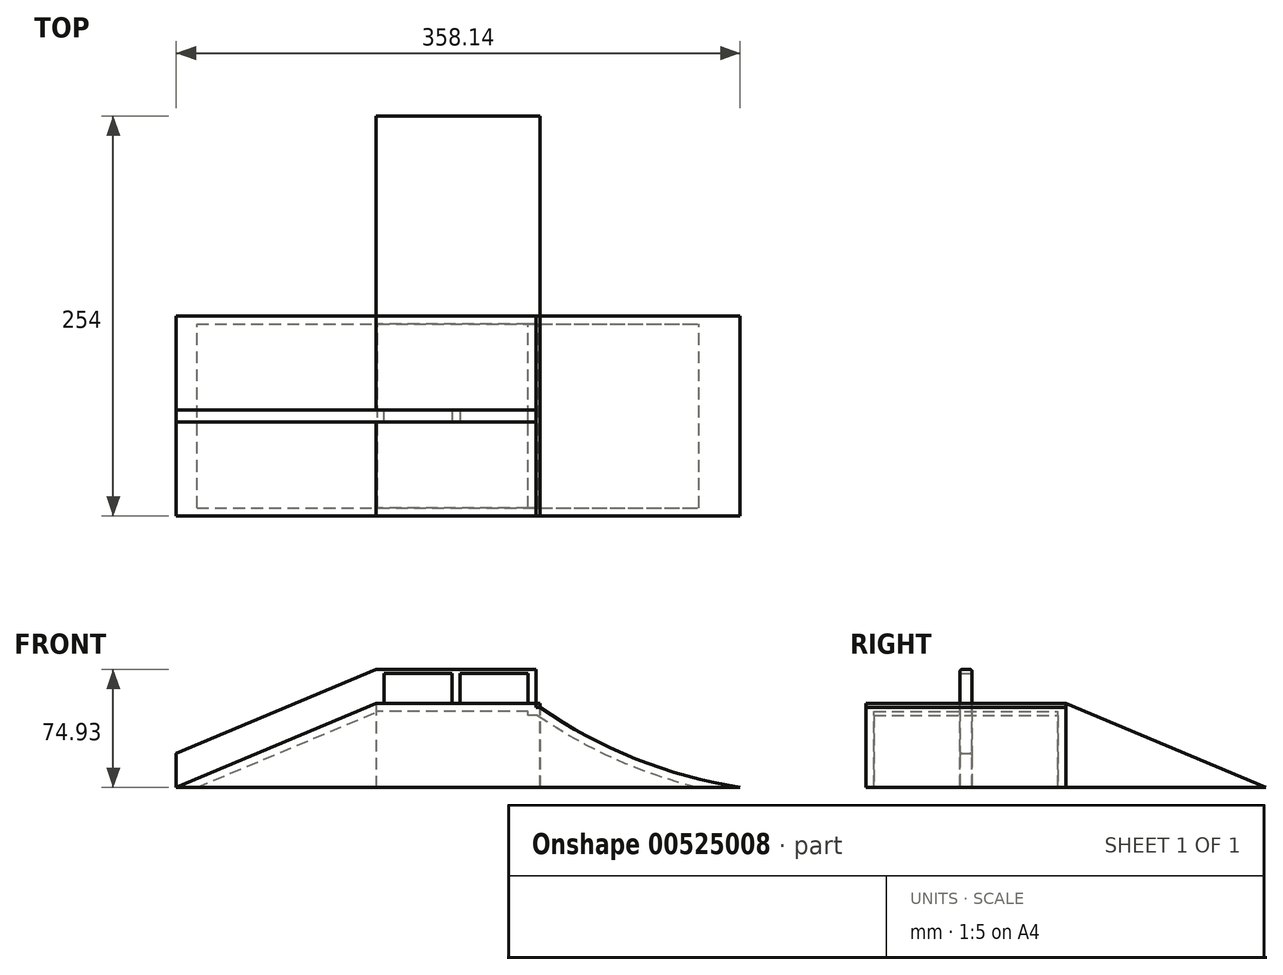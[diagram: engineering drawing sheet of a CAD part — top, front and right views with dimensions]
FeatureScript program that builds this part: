
annotation { "Feature Type Name" : "Feature", "Feature Type Description" : "" }
export const myFeature = defineFeature(function(context is Context, id is Id, definition is map)
    precondition{}
    {
        {
            var Q0;
            Q0=qCreatedBy(makeId("Front.planeOp"),FACE);
            var sketch = newSketch(context, id + "F0", { "sketchPlane" : qUnion([Q0])});
            skLineSegment(sketch, "E0.bottom", {"start": v(0, 0) * mm, "end": v(127, 0) * mm});
            skLineSegment(sketch, "E0.left", {"start": v(0, 0) * mm, "end": v(0, 50.8) * mm});
            skArc(sketch, "E1", {"start": v(0, 50.8) * mm, "mid": v(60.61, 18.18) * mm, "end": v(127, 0) * mm});
            skLineSegment(sketch, "E2.bottom", {"start": v(0, 0) * mm, "end": v(-2.54, 0) * mm});
            skLineSegment(sketch, "E2.top", {"start": v(0, 50.8) * mm, "end": v(-2.54, 50.8) * mm});
            skLineSegment(sketch, "E2.right", {"start": v(-2.54, 0) * mm, "end": v(-2.54, 50.8) * mm});
            skLineSegment(sketch, "E3.bottom", {"start": v(-2.54, 0) * mm, "end": v(-104.14, 0) * mm});
            skLineSegment(sketch, "E3.top", {"start": v(-2.54, 53.34) * mm, "end": v(-104.14, 53.34) * mm});
            skLineSegment(sketch, "E3.left", {"start": v(-2.54, 0) * mm, "end": v(-2.54, 53.34) * mm});
            skLineSegment(sketch, "E3.right", {"start": v(-104.14, 0) * mm, "end": v(-104.14, 53.34) * mm});
            skCircle(sketch, "E4", {"center": v(-1.27, 52.07) * mm, "radius": 1.27 * mm});
            skPoint(sketch, "E4.centerSnap0", {"position": v(-1.27, 50.8) * mm});
            skLineSegment(sketch, "E5", {"start": v(-104.14, 0) * mm, "end": v(-231.14, 0) * mm});
            skLineSegment(sketch, "E6", {"start": v(-231.14, 0) * mm, "end": v(-104.14, 53.34) * mm});
            skSolve(sketch);
        }
        {
            var Q0;
            Q0=makeQuery(id+"F0.imprint","IMPRINT",FACE,{"disambiguationData":[TD([[makeQuery(id+"F0.imprint","IMPRINT",EDGE,{"derivedFrom":sQuery(id+"F0.wireOp",EDGE,"E0.bottom")}),1.0]])]});
            var Q1;
            Q1=makeQuery(id+"F0.imprint","IMPRINT",FACE,{"disambiguationData":[TD([[makeQuery(id+"F0.imprint","IMPRINT",EDGE,{"derivedFrom":sQuery(id+"F0.wireOp",EDGE,"gSf4ow2M-3nON-57kk-JyT3-ZSVy4p9OPfto.bottom")}),-1.0]])]});
            var Q2;
            {var subQ3=sQuery(id+"F0.wireOp",EDGE,"E3.bottom");Q2=makeQuery(id+"F0.imprint","IMPRINT",FACE,{"disambiguationData":[TD([[makeQuery(id+"F0.imprint","IMPRINT",EDGE,{"derivedFrom":subQ3}),-1.0]])]});}
            var Q3;
            {var subQ5=sQuery(id+"F0.wireOp",EDGE,"E2.bottom");Q3=makeQuery(id+"F0.imprint","IMPRINT",FACE,{"disambiguationData":[TD([[makeQuery(id+"F0.imprint","IMPRINT",EDGE,{"derivedFrom":subQ5}),-1.0]])]});}
            var Q4;
            {var subQ0=sQuery(id+"F0.wireOp",EDGE,"E4");var subQ1=makeQuery(id+"F0.imprint","INTERSECT",VERTEX,{"derivedFrom":[sQuery(id+"F0.wireOp",EDGE,"E2.top"),subQ0]});Q4=makeQuery(id+"F0.imprint","IMPRINT",FACE,{"disambiguationData":[TD([[makeQuery(id+"F0.imprint","IMPRINT",EDGE,{"disambiguationData":[TD([[subQ1,1.0]])],"derivedFrom":subQ0}),1.0]])]});}
            var Q5;
            Q5=makeQuery(id+"F0.imprint","IMPRINT",FACE,{"disambiguationData":[TD([[makeQuery(id+"F0.imprint","IMPRINT",EDGE,{"derivedFrom":sQuery(id+"F0.wireOp",EDGE,"E3.right")}),1.0]])]});
            extrude(context, id + "F1", {"entities" : qUnion([Q0, Q1, Q2, Q3, Q4, Q5]), "depth" : 127 * mm});
        }
        {
            var Q0;
            Q0=makeQuery(id+"F1.opExtrude","SWEPT_FACE",FACE,{"disambiguationData":[OSD([sQuery(id+"F0.wireOp",EDGE,"E3.top")])]});
            var sketch = newSketch(context, id + "F2", { "sketchPlane" : qUnion([Q0])});
            skLineSegment(sketch, "E7.bottom", {"start": v(-104.14, -67.31) * mm, "end": v(-99.06, -67.31) * mm});
            skLineSegment(sketch, "E7.top", {"start": v(-104.14, -59.7) * mm, "end": v(-99.06, -59.7) * mm});
            skLineSegment(sketch, "E7.left", {"start": v(-104.14, -67.31) * mm, "end": v(-104.14, -59.7) * mm});
            skLineSegment(sketch, "E7.right", {"start": v(-99.06, -67.31) * mm, "end": v(-99.06, -59.7) * mm});
            skLineSegment(sketch, "E8.bottom", {"start": v(-2.54, -67.3) * mm, "end": v(-7.62, -67.3) * mm});
            skLineSegment(sketch, "E8.top", {"start": v(-2.54, -59.7) * mm, "end": v(-7.62, -59.7) * mm});
            skLineSegment(sketch, "E8.left", {"start": v(-2.54, -67.3) * mm, "end": v(-2.54, -59.7) * mm});
            skLineSegment(sketch, "E8.right", {"start": v(-7.62, -67.3) * mm, "end": v(-7.62, -59.7) * mm});
            skLineSegment(sketch, "E9.bottom", {"start": v(-55.88, -59.7) * mm, "end": v(-50.8, -59.7) * mm});
            skLineSegment(sketch, "E9.top", {"start": v(-55.88, -67.31) * mm, "end": v(-50.8, -67.31) * mm});
            skLineSegment(sketch, "E9.left", {"start": v(-55.88, -59.7) * mm, "end": v(-55.88, -67.31) * mm});
            skLineSegment(sketch, "E9.right", {"start": v(-50.8, -59.7) * mm, "end": v(-50.8, -67.31) * mm});
            skSolve(sketch);
        }
        {
            var Q0;
            Q0=qSketchRegion(id+"F2",true);
            extrude(context, id + "F3", {"entities" : qUnion([Q0]), "operationType" : NewBodyOperationType.ADD, "depth" : 19.05 * mm});
        }
        {
            var Q0;
            Q0=makeQuery(id+"F3.boolean.opBoolean","MERGE",FACE,{"derivedFrom":[makeQuery(id+"F1.opExtrude","SWEPT_FACE",FACE,{"disambiguationData":[OSD([sQuery(id+"F0.wireOp",EDGE,"E3.left")])]}),makeQuery(id+"F3.opExtrude","SWEPT_FACE",FACE,{"disambiguationData":[OSD([sQuery(id+"F2.wireOp",EDGE,"E8.left")])]})]});
            var sketch = newSketch(context, id + "F4", { "sketchPlane" : qUnion([Q0])});
            skLineSegment(sketch, "E10.bottom", {"start": v(-67.3, 72.4) * mm, "end": v(-59.7, 72.4) * mm});
            skLineSegment(sketch, "E10.top", {"start": v(-67.3, 74.93) * mm, "end": v(-59.7, 74.93) * mm});
            skLineSegment(sketch, "E10.left", {"start": v(-67.3, 72.4) * mm, "end": v(-67.3, 74.93) * mm});
            skLineSegment(sketch, "E10.right", {"start": v(-59.7, 72.4) * mm, "end": v(-59.7, 74.93) * mm});
            skSolve(sketch);
        }
        {
            var Q0;
            Q0=makeQuery(id+"F4.imprint","IMPRINT",FACE,{"disambiguationData":[TD([[makeQuery(id+"F4.imprint","IMPRINT",EDGE,{"derivedFrom":sQuery(id+"F4.wireOp",EDGE,"E10.bottom")}),1.0]])]});
            extrude(context, id + "F5", {"entities" : qUnion([Q0]), "operationType" : NewBodyOperationType.ADD, "oppositeDirection" : true, "depth" : 101.6 * mm});
        }
        {
            var Q0;
            Q0=makeQuery(id+"F1.opExtrude","SWEPT_FACE",FACE,{"disambiguationData":[OSD([sQuery(id+"F0.wireOp",EDGE,"E0.bottom"),sQuery(id+"F0.wireOp",EDGE,"E2.bottom"),sQuery(id+"F0.wireOp",EDGE,"E3.bottom"),sQuery(id+"F0.wireOp",EDGE,"E5")])]});
            shell(context, id + "F6", {"entities" : qUnion([Q0]), "thickness" : 5.08 * mm});
        }
        {
            var Q0;
            Q0=makeQuery(id+"F5.boolean.opBoolean","MERGE",FACE,{"derivedFrom":[makeQuery(id+"F3.opExtrude","SWEPT_FACE",FACE,{"disambiguationData":[OSD([sQuery(id+"F2.wireOp",EDGE,"E7.top")])]}),makeQuery(id+"F3.opExtrude","SWEPT_FACE",FACE,{"disambiguationData":[OSD([sQuery(id+"F2.wireOp",EDGE,"E8.top")])]}),makeQuery(id+"F3.opExtrude","SWEPT_FACE",FACE,{"disambiguationData":[OSD([sQuery(id+"F2.wireOp",EDGE,"E9.bottom")])]}),makeQuery(id+"F5.opExtrude","SWEPT_FACE",FACE,{"disambiguationData":[OSD([sQuery(id+"F4.wireOp",EDGE,"E10.right")])]})]});
            var sketch = newSketch(context, id + "F7", { "sketchPlane" : qUnion([Q0])});
            skLineSegment(sketch, "E11", {"start": v(104.14, 74.93) * mm, "end": v(231.14, 21.59) * mm});
            skLineSegment(sketch, "E12", {"start": v(231.14, 21.59) * mm, "end": v(231.14, 0) * mm});
            skLineSegment(sketch, "E13", {"start": v(231.14, 0) * mm, "end": v(104.14, 53.34) * mm});
            skLineSegment(sketch, "E14", {"start": v(104.14, 74.93) * mm, "end": v(104.14, 53.34) * mm});
            skSolve(sketch);
        }
        {
            var Q0;
            Q0=qSketchRegion(id+"F7",true);
            extrude(context, id + "F8", {"entities" : qUnion([Q0]), "operationType" : NewBodyOperationType.ADD, "oppositeDirection" : true, "depth" : 7.62 * mm});
        }
        {
            var Q0;
            Q0=qCreatedBy(makeId("Right.planeOp"),FACE);
            var sketch = newSketch(context, id + "F9", { "sketchPlane" : qUnion([Q0])});
            skLineSegment(sketch, "E15", {"start": v(0, 53.34) * mm, "end": v(127, 0) * mm});
            skLineSegment(sketch, "E16", {"start": v(127, 0) * mm, "end": v(0, 0) * mm});
            skLineSegment(sketch, "E17", {"start": v(0, 0) * mm, "end": v(0, 53.34) * mm});
            skSolve(sketch);
        }
        {
            var Q0;
            Q0=makeQuery(id+"F9.imprint","IMPRINT",FACE,{"disambiguationData":[TD([[makeQuery(id+"F9.imprint","IMPRINT",EDGE,{"derivedFrom":sQuery(id+"F9.wireOp",EDGE,"E15")}),-1.0]])]});
            extrude(context, id + "F10", {"entities" : qUnion([Q0]), "oppositeDirection" : true, "depth" : 104.14 * mm});
        }
        {
            var Q0;
            Q0=makeQuery(id+"F5.opExtrude","SWEPT_EDGE",EDGE,{"disambiguationData":[OSD([sQuery(id+"F4.wireOp",EDGE,"E10.top"),sQuery(id+"F4.wireOp",EDGE,"E10.left")])]});
            var Q1;
            Q1=makeQuery(id+"F8.opExtrude","CAP_EDGE",EDGE,{"disambiguationData":[OSD([sQuery(id+"F7.wireOp",EDGE,"E11")])],"isStart":false});
            var Q2;
            {var subQ0=sQuery(id+"F4.wireOp",EDGE,"E10.top");Q2=makeQuery(id+"F8.boolean.opBoolean","MERGE",EDGE,{"derivedFrom":[makeQuery(id+"F5.opExtrude","CAP_EDGE",EDGE,{"disambiguationData":[OSD([subQ0])],"isStart":false}),makeQuery(id+"F8.opExtrude","SWEPT_EDGE",EDGE,{"disambiguationData":[OSD([subQ0,sQuery(id+"F4.wireOp",EDGE,"E10.right"),sQuery(id+"F7.wireOp",EDGE,"E11"),sQuery(id+"F7.wireOp",EDGE,"E14")])]})]});}
            var Q3;
            Q3=makeQuery(id+"F8.opExtrude","CAP_EDGE",EDGE,{"disambiguationData":[OSD([sQuery(id+"F7.wireOp",EDGE,"E11")])],"isStart":true});
            var Q4;
            Q4=makeQuery(id+"F5.opExtrude","SWEPT_EDGE",EDGE,{"disambiguationData":[OSD([sQuery(id+"F4.wireOp",EDGE,"E10.top"),sQuery(id+"F4.wireOp",EDGE,"E10.right")])]});
            fillet(context, id + "F11", {"entities" : qUnion([Q0, Q1, Q2, Q3, Q4]), "radius" : 1.27 * mm, "tangentPropagation" : true, "allowEdgeOverflow" : false});
        }
    });
